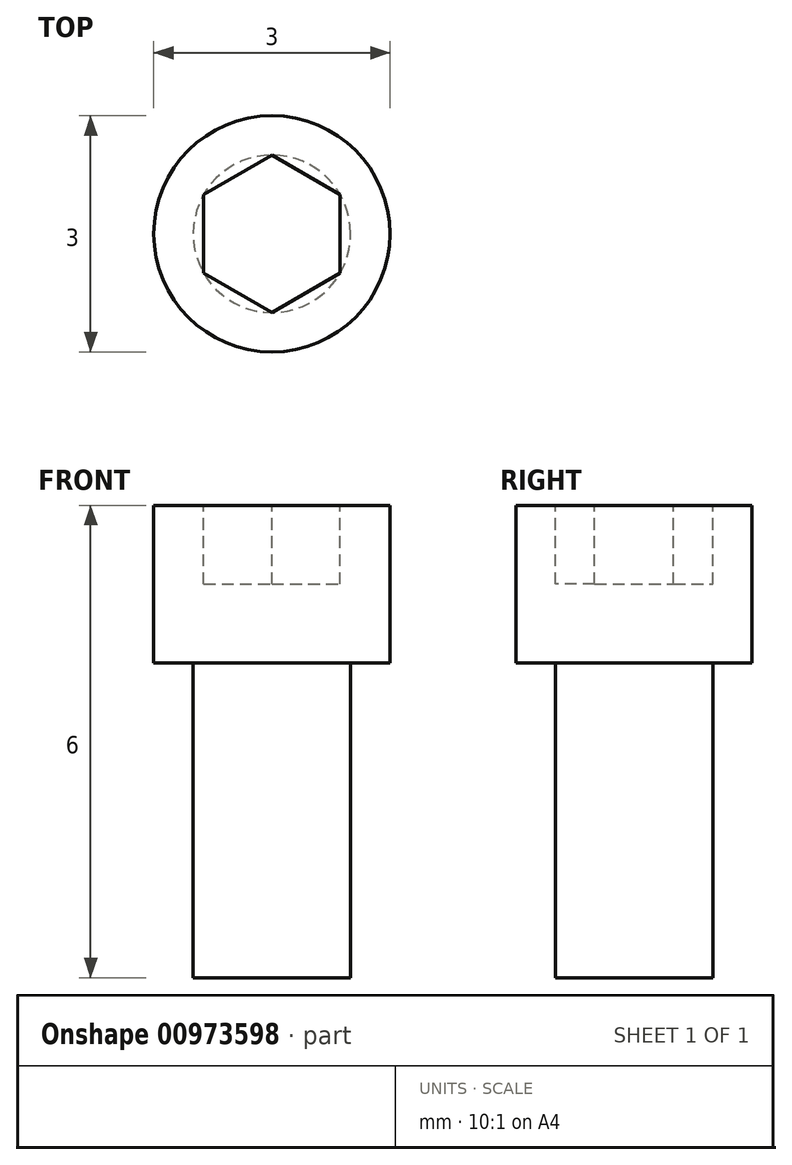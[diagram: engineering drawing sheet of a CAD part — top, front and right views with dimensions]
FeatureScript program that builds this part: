
annotation { "Feature Type Name" : "Feature", "Feature Type Description" : "" }
export const myFeature = defineFeature(function(context is Context, id is Id, definition is map)
    precondition{}
    {
        {
            var Q0;
            Q0=qCreatedBy(makeId("Top.planeOp"),FACE);
            var sketch = newSketch(context, id + "F0", { "sketchPlane" : qUnion([Q0])});
            skCircle(sketch, "E0", {"center": v(0, 0) * mm, "radius": 1 * mm});
            skSolve(sketch);
        }
        {
            var Q0;
            Q0 = qSketchRegion(id + "F0", true);
            extrude(context, id + "F1", {"entities" : qUnion([Q0]), "depth" : 4 * mm, "offsetDistance" : 25 * mm});
        }
        {
            var Q0;
            Q0=makeQuery(id+"F1.opExtrude","CAP_FACE",FACE,{"disambiguationData":[OSD([sQuery(id+"F0.wireOp",EDGE,"E0")])],"isStart":false});
            var sketch = newSketch(context, id + "F2", { "sketchPlane" : qUnion([Q0])});
            skCircle(sketch, "E1", {"center": v(0, 0) * mm, "radius": 1.5 * mm});
            skSolve(sketch);
        }
        {
            var Q0;
            Q0 = qSketchRegion(id + "F2", true);
            extrude(context, id + "F3", {"entities" : qUnion([Q0]), "operationType" : NewBodyOperationType.ADD, "depth" : 2 * mm, "offsetDistance" : 25 * mm});
        }
        {
            var Q0;
            Q0=makeQuery(id+"F3.opExtrude","CAP_FACE",FACE,{"disambiguationData":[OSD([sQuery(id+"F2.wireOp",EDGE,"E1")])],"isStart":false});
            var sketch = newSketch(context, id + "F4", { "sketchPlane" : qUnion([Q0])});
            skLineSegment(sketch, "E2", {"start": v(0, 1.5) * mm, "end": v(0, -1.5) * mm, "construction": true});
            skLineSegment(sketch, "E3", {"start": v(-1.5, 0) * mm, "end": v(1.5, 0) * mm, "construction": true});
            skLineSegment(sketch, "E4", {"start": v(0, -1) * mm, "end": v(0.87, -0.5) * mm});
            skLineSegment(sketch, "E5", {"start": v(0.87, -0.5) * mm, "end": v(0.87, 0.5) * mm});
            skLineSegment(sketch, "E6", {"start": v(0.87, 0.5) * mm, "end": v(0, 1) * mm});
            skLineSegment(sketch, "E7", {"start": v(0, 1) * mm, "end": v(-0.87, 0.5) * mm});
            skLineSegment(sketch, "E8", {"start": v(-0.87, 0.5) * mm, "end": v(-0.87, -0.5) * mm});
            skLineSegment(sketch, "E9", {"start": v(-0.87, -0.5) * mm, "end": v(0, -1) * mm});
            skSolve(sketch);
        }
        {
            var Q0;
            Q0 = qSketchRegion(id + "F4", true);
            extrude(context, id + "F5", {"entities" : qUnion([Q0]), "operationType" : NewBodyOperationType.REMOVE, "oppositeDirection" : true, "depth" : 1 * mm, "offsetDistance" : 25 * mm});
        }
    });
